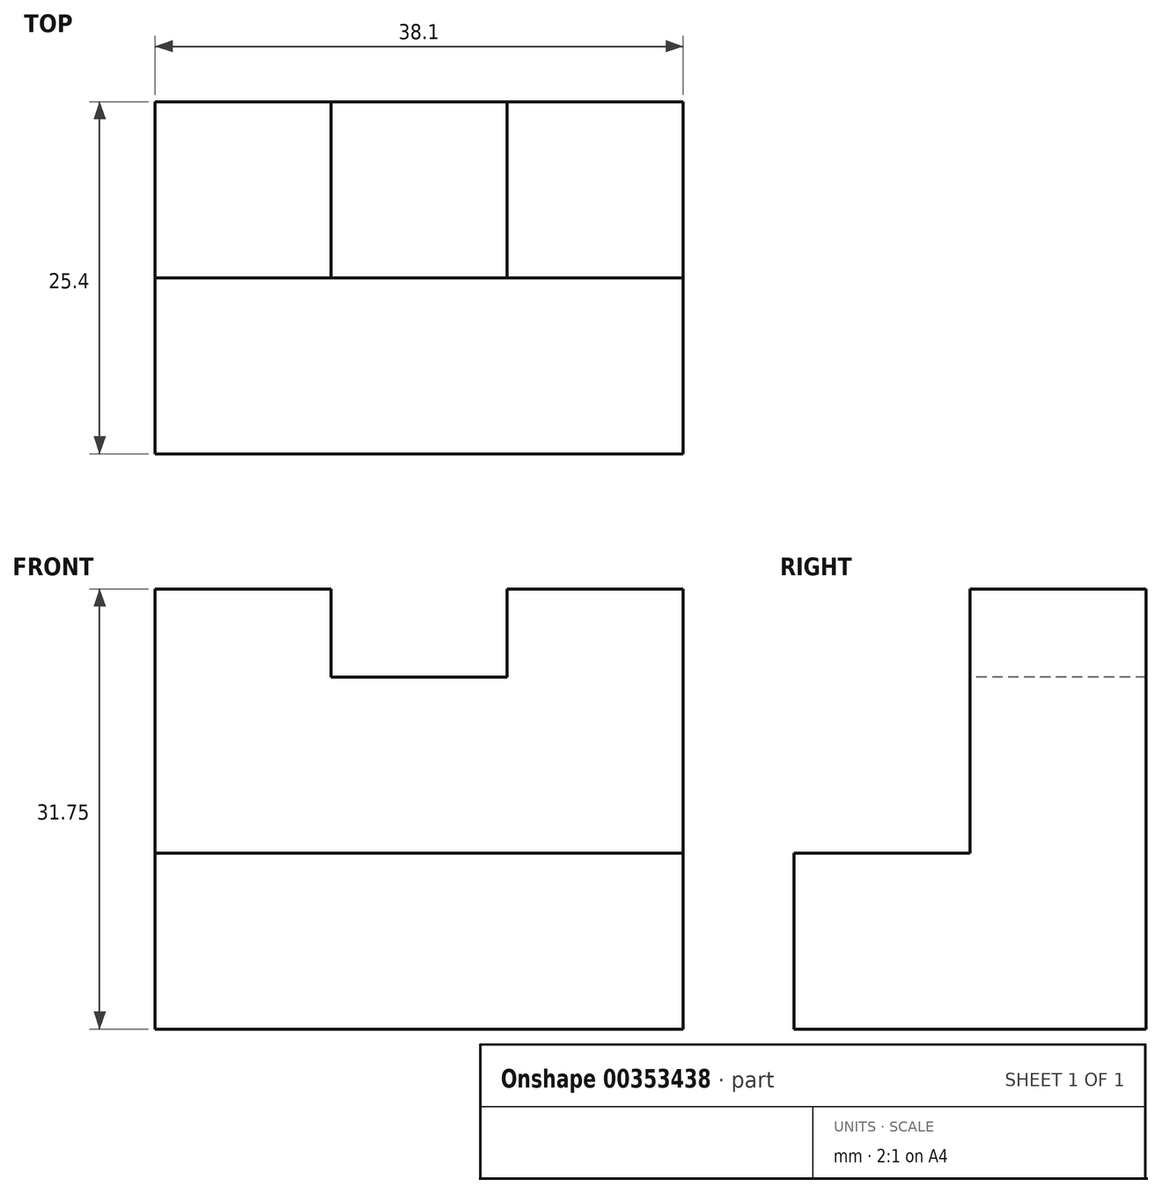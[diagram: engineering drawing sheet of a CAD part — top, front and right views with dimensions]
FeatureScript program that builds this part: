
annotation { "Feature Type Name" : "Feature", "Feature Type Description" : "" }
export const myFeature = defineFeature(function(context is Context, id is Id, definition is map)
    precondition{}
    {
        {
            var Q0;
            Q0=qCreatedBy(makeId("Right.planeOp"),FACE);
            var sketch = newSketch(context, id + "F0", { "sketchPlane" : qUnion([Q0])});
            skLineSegment(sketch, "E0", {"start": v(0, 0) * mm, "end": v(25.4, 0) * mm});
            skLineSegment(sketch, "E1", {"start": v(25.4, 0) * mm, "end": v(25.4, 31.75) * mm});
            skLineSegment(sketch, "E2", {"start": v(25.4, 31.75) * mm, "end": v(12.7, 31.75) * mm});
            skLineSegment(sketch, "E3", {"start": v(12.7, 31.75) * mm, "end": v(12.7, 12.7) * mm});
            skLineSegment(sketch, "E4", {"start": v(12.7, 12.7) * mm, "end": v(0, 12.7) * mm});
            skLineSegment(sketch, "E5", {"start": v(0, 12.7) * mm, "end": v(0, 0) * mm});
            skSolve(sketch);
        }
        {
            var Q0;
            Q0 = qSketchRegion(id + "F0", true);
            extrude(context, id + "F1", {"entities" : qUnion([Q0]), "oppositeDirection" : true, "depth" : 38.1 * mm});
        }
        {
            var Q0;
            Q0=makeQuery(id+"F1.opExtrude","SWEPT_FACE",FACE,{"disambiguationData":[OSD([sQuery(id+"F0.wireOp",EDGE,"E3")])]});
            var sketch = newSketch(context, id + "F2", { "sketchPlane" : qUnion([Q0])});
            skLineSegment(sketch, "E6", {"start": v(-38.1, 31.75) * mm, "end": v(-25.4, 31.75) * mm});
            skLineSegment(sketch, "E7", {"start": v(-25.4, 31.75) * mm, "end": v(-25.4, 25.4) * mm});
            skLineSegment(sketch, "E8", {"start": v(-25.4, 25.4) * mm, "end": v(-12.7, 25.4) * mm});
            skLineSegment(sketch, "E9", {"start": v(-12.7, 25.4) * mm, "end": v(-12.7, 31.75) * mm});
            skSolve(sketch);
        }
        {
            var Q0;
            Q0 = qSketchRegion(id + "F2", true);
            var Q1;
            {var subQ0=sQuery(id+"F2.wireOp",EDGE,"E7");Q1=makeQuery(id+"F2.imprint","IMPRINT",FACE,{"disambiguationData":[TD([[makeQuery(id+"F2.imprint","IMPRINT",EDGE,{"derivedFrom":subQ0}),1.0]])]});}
            extrude(context, id + "F3", {"entities" : qUnion([Q0, Q1]), "operationType" : NewBodyOperationType.REMOVE, "oppositeDirection" : true, "depth" : 25.4 * mm});
        }
    });
